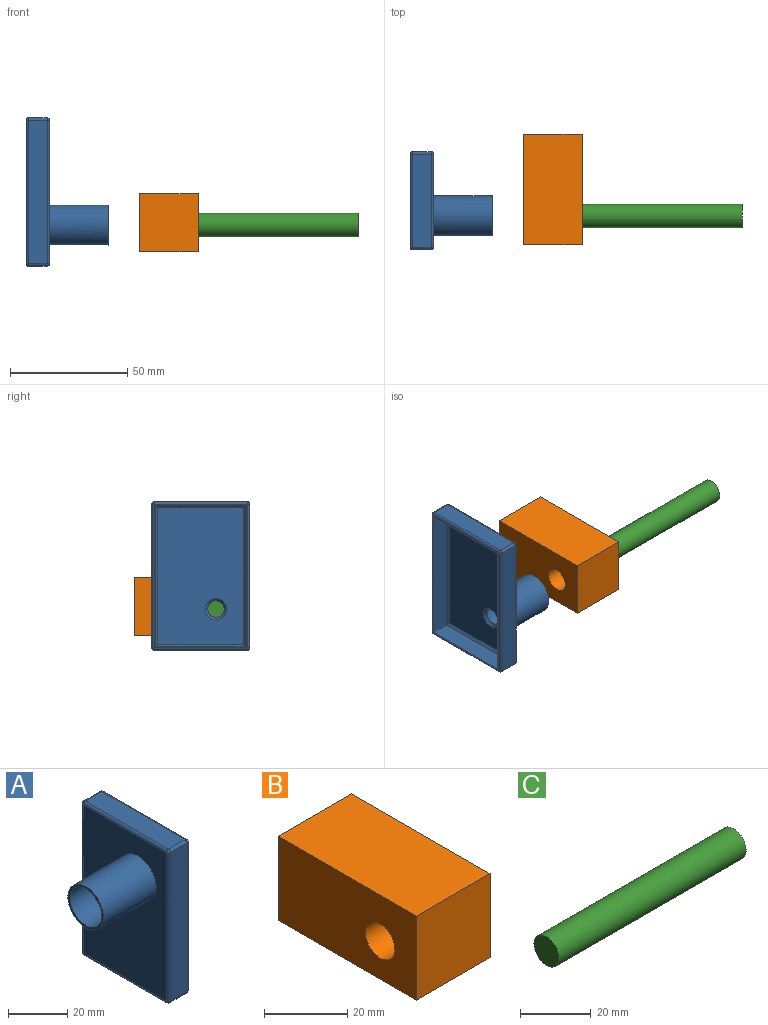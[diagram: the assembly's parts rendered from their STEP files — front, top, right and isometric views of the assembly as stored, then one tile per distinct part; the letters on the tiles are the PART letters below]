
ASSEMBLY  parts=3 mates=3
PART A: 41 faces, bbox 35x41.6x63.2 mm
  f0: plane 15x15mm, normal (-1,0,0), area 138.2mm2, adj f12,f38
  f1: plane 61.18x39.59mm, normal (1,0,0), area 99.8mm2, adj f7,f8,f9,f10,f16,f17,f26,f27
  f2: plane 39.59x8mm, normal (0,0,-1), area 316.7mm2, adj f21,f26,f29,f32
  f3: plane 61.18x8mm, normal (0,1,0), area 489.5mm2, adj f18,f27,f28,f32
  f4: plane 39.59x8mm, normal (0,0,1), area 316.7mm2, adj f13,f17,f18,f19
  f5: plane 61.18x8mm, normal (0,-1,0), area 489.5mm2, adj f13,f16,f20,f21
  f6: plane 61.18x39.59mm, normal (-1,0,0), area 2195.3mm2, adj f19,f20,f28,f29,f39
  f7: plane 38.59x7.5mm, normal (0,0,1), area 289.4mm2, adj f1,f8,f10,f36
  f8: plane 60.18x7.5mm, normal (0,-1,0), area 451.4mm2, adj f1,f7,f9,f34
  f9: plane 38.59x7.5mm, normal (0,0,-1), area 289.4mm2, adj f1,f8,f10,f35
  f10: plane 60.18x7.5mm, normal (0,1,0), area 451.4mm2, adj f1,f7,f9,f37
  f11: plane 58.18x36.59mm, normal (1,0,0), area 2065.3mm2, adj f33,f34,f35,f36,f37
  f12: cylinder r=3.5mm len=7mm, axis (1,0,0), area 11mm2, adj f0,f33
  f13: cylinder r=1mm len=8mm, axis (-1,0,0), area 12.6mm2, adj f4,f5,f14,f15
  f14: sphere r=1mm, area 1.6mm2, adj f13,f16,f17
  f15: sphere r=1mm, area 1.6mm2, adj f13,f19,f20
  f16: cylinder r=1mm len=61.18mm, axis (0,0,1), area 96.1mm2, adj f1,f5,f14,f22
  f17: cylinder r=1mm len=39.59mm, axis (0,1,0), area 62.2mm2, adj f1,f4,f14,f23
  f18: cylinder r=1mm len=8mm, axis (1,0,0), area 12.6mm2, adj f3,f4,f23,f24
  f19: cylinder r=1mm len=39.59mm, axis (0,-1,0), area 62.2mm2, adj f4,f6,f15,f24
  f20: cylinder r=1mm len=61.18mm, axis (0,0,-1), area 96.1mm2, adj f5,f6,f15,f25
  f21: cylinder r=1mm len=8mm, axis (1,0,0), area 12.6mm2, adj f2,f5,f22,f25
  f22: sphere r=1mm, area 1.6mm2, adj f16,f21,f26
  f23: sphere r=1mm, area 1.6mm2, adj f17,f18,f27
  f24: sphere r=1mm, area 1.6mm2, adj f18,f19,f28
  f25: sphere r=1mm, area 1.6mm2, adj f20,f21,f29
  f26: cylinder r=1mm len=39.59mm, axis (0,-1,0), area 62.2mm2, adj f1,f2,f22,f30
  f27: cylinder r=1mm len=61.18mm, axis (0,0,-1), area 96.1mm2, adj f1,f3,f23,f30
  f28: cylinder r=1mm len=61.18mm, axis (0,0,1), area 96.1mm2, adj f3,f6,f24,f31
  f29: cylinder r=1mm len=39.59mm, axis (0,1,0), area 62.2mm2, adj f2,f6,f25,f31
  f30: sphere r=1mm, area 1.6mm2, adj f26,f27,f32
  f31: sphere r=1mm, area 1.6mm2, adj f28,f29,f32
  f32: cylinder r=1mm len=8mm, axis (-1,0,0), area 12.6mm2, adj f2,f3,f30,f31
  f33: cone r=3.5mm half-angle=45deg, axis (1,0,0), area 35.5mm2, adj f11,f12
  f34: plane 60.18x1mm, normal (0.71,-0.71,0), area 83.7mm2, adj f8,f11,f35,f36
  f35: plane 38.59x1mm, normal (0.71,0,-0.71), area 53.2mm2, adj f9,f11,f34,f37
  f36: plane 38.59x1mm, normal (0.71,0,0.71), area 53.2mm2, adj f7,f11,f34,f37
  f37: plane 60.18x1mm, normal (0.71,0.71,0), area 83.7mm2, adj f10,f11,f35,f36
  f38: cylinder r=7.5mm len=25mm, axis (1,0,0), area 1178.1mm2, adj f0,f40
  f39: cylinder r=8.5mm len=25mm, axis (1,0,0), area 1335.2mm2, adj f6,f40
  f40: plane 17x17mm, normal (-1,0,0), area 50.3mm2, adj f38,f39
PART B: 7 faces, bbox 25x47x24.7 mm
  f0: plane 47x25mm, normal (0,0,-1), area 1174.9mm2, adj f1,f4,f5,f6
  f1: plane 25x24.71mm, normal (0,1,0), area 617.7mm2, adj f0,f2,f5,f6
  f2: plane 47x25mm, normal (0,0,1), area 1174.9mm2, adj f1,f4,f5,f6
  f3: cylinder r=5mm len=25mm, axis (-1,0,0), area 785.4mm2, adj f5,f6
  f4: plane 25x24.71mm, normal (0,-1,0), area 617.7mm2, adj f0,f2,f5,f6
  f5: plane 47x24.71mm, normal (1,0,0), area 1082.7mm2, adj f0,f1,f2,f3,f4
  f6: plane 47x24.71mm, normal (-1,0,0), area 1082.7mm2, adj f0,f1,f2,f3,f4
PART C: 3 faces, bbox 75x10x10 mm
  f0: cylinder r=5mm len=75mm, axis (-1,0,0), area 2356.2mm2, adj f1,f2
  f1: plane 10x10mm, normal (-1,0,0), area 78.5mm2, adj f0
  f2: plane 10x10mm, normal (1,0,0), area 78.5mm2, adj f0
PLACE A rot(axis=(0,-1,0),180deg) t=(8.56,-57.69,-81.6)mm
PLACE B t=(46.87,20.61,-6.2)mm fixed
PLACE C t=(64.86,34.93,-38.81)mm
MATE parallel B.f0 <-> A.f4  axis (0,0,-1) through (59.37,-17.06,-71.16)mm
MATE cylindrical A.f12 <-> B.f3  axis (-1,0,0) through (33.56,-28.26,-59.9)mm
MATE slider C.f0 <-> B.f3  axis (-1,0,0) through (102.36,-28.26,-59.9)mm
